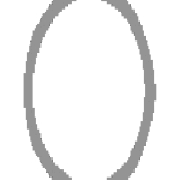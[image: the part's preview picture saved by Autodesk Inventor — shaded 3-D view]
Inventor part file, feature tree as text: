
AUTODESK INVENTOR PART (.ipt)
format: ipt  version: 2021 (Build 250183000, 183)  size: 110,080 bytes
history: native  units: in
note: dims shown in document units (in); Inventor stores cm internally (conversion verified against a paired STEP export)
features: other x4, sketch x3, plane x1
ambient origin geometry x8: Origin, YZ Plane, XZ Plane, XY Plane, X Axis, Y Axis, Z Axis, Center Point
bodies: Solid1 (feature_tree), Body (feature_tree)
feature tree (8):
  other  "Driven Length"
  other  "Frame Generator"
  other  "Start Plane"
  other  "End Plane"
  sketch  "Sketch"  dims[d2=16.0833in d4=-0.0in d5=16.0833in d6=0.12in d7=0.0in d10=90.0deg d9=16.0833in]
  sketch  "Sketch4"  dims[d0=1.0in]
  plane  "Work Plane4"
  sketch  "Sketch5"  dims[d1=0.065in]
